# Revit family: G6 PLM MS652119PM-V2
name_source: partatom
category: Datengeräte
units: mm (PartAtom-declared; Revit-internal decimal feet)

## family parameters
Arbeitsebenenbasiert = Nein
Beim Laden mit Abzugskörper schneiden = Nein
Bemaßung runder Anschluss = Durchmesser verwenden
Beschriftungsausrichtung beibehalten = Nein
Gemeinsam genutzt = Nein
Immer vertikal = Ja
OmniClass-Nummer = 23.85.50.17
OmniClass-Titel = Communication and Data Processing Equipment
Raumberechnungspunkt = Nein
Teiletyp = Normal

## types (1)
- MS652119PM-V2
    Artikelnummer = MS652119PM-V2
    Beschreibung = 13 Port GBE Industrial PLM Switch PoE+
    Hersteller = MICROSENS
    Interface 1 = 4 x 100/1000X SFP-Slots / 10/100/1000T (Combo)
    Interface 10 = RS-232 Port (RJ-45)
    Interface 2 = 9 x 10/100/1000T
    Interface 3 = 8 x PoE+
    Interface 4 = 1 x PD
    Interface 5 = 2 x 24..57VDC
    Interface 6 = DIN-Rail
    Interface 7 = USB
    Interface 8 = SD-Card incl.
    Interface 9 = 2 x I/O
    Property 1 = Managed switch
    Vorgabe-Ansicht = 0 mm  [stored 0 ft]

note: [stored X ft] marks values corroborated as IEEE doubles in the binary element streams (Revit-internal decimal feet)
